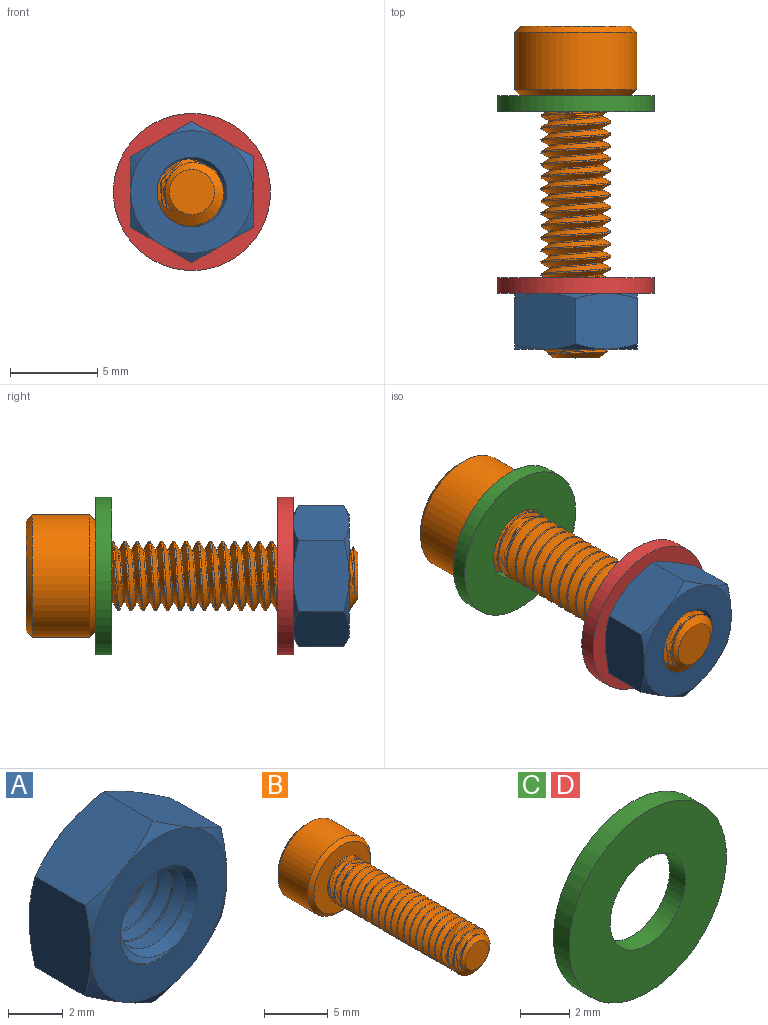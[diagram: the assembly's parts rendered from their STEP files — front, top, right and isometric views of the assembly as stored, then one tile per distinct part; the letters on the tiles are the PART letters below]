
ASSEMBLY  parts=4 mates=3
PART A: 26 faces, bbox 8.4x4.2x8.4 mm
  f0: plane 3.83x3.54mm, normal (-0.5,0,0.87), area 12.1mm2, adj f1,f5,f17,f18,f21,f22
  f1: plane 4.38x3.54mm, normal (-1,0,0), area 12.1mm2, adj f0,f2,f16,f17,f22,f23
  f2: plane 3.83x3.54mm, normal (-0.5,0,-0.87), area 12.1mm2, adj f1,f3,f15,f16,f23,f24
  f3: plane 3.83x3.54mm, normal (0.5,0,-0.87), area 12.1mm2, adj f2,f4,f14,f15,f24,f25
  f4: plane 4.38x3.54mm, normal (1,0,0), area 12.1mm2, adj f3,f5,f14,f19,f20,f25
  f5: plane 3.83x3.54mm, normal (0.5,0,0.87), area 12.1mm2, adj f0,f4,f18,f19,f20,f21
  f6: plane 7x7mm, normal (0,-1,0), area 25.9mm2, adj f8,f13,f14,f15,f16,f17,f18,f19
  f7: plane 7x7mm, normal (0,1,0), area 25.9mm2, adj f9,f13,f20,f21,f22,f23,f24,f25
  f8: cone r=2mm half-angle=45deg, axis (0,-1,0), area 3.7mm2, adj f6,f10,f11,f12
  f9: cone r=2mm half-angle=45deg, axis (0,1,0), area 3.7mm2, adj f7,f10,f11,f12
  f10: bspline ~4.62x4mm, area 23.1mm2, adj f8,f9,f12,f13
  f11: bspline ~4.62x4mm, area 23.1mm2, adj f8,f9,f12,f13
  f12: cylinder r=1.55mm len=3.09mm, axis (0,1,0), area 2.7mm2, adj f8,f9,f10,f11
  f13: cylinder r=2mm len=4mm, axis (0,1,0), area 5.1mm2, adj f6,f7,f10,f11
  f14: cone r=3.5mm half-angle=60deg, axis (0,1,0), area 1.2mm2, adj f3,f4,f6
  f15: cone r=3.5mm half-angle=60deg, axis (0,1,0), area 1.2mm2, adj f2,f3,f6
  f16: cone r=3.5mm half-angle=60deg, axis (0,1,0), area 1.2mm2, adj f1,f2,f6
  f17: cone r=3.5mm half-angle=60deg, axis (0,1,0), area 1.2mm2, adj f0,f1,f6
  f18: cone r=3.5mm half-angle=60deg, axis (0,1,0), area 1.2mm2, adj f0,f5,f6
  f19: cone r=3.5mm half-angle=60deg, axis (0,1,0), area 1.2mm2, adj f4,f5,f6
  f20: cone r=3.5mm half-angle=60deg, axis (0,-1,0), area 1.2mm2, adj f4,f5,f7
  f21: cone r=3.5mm half-angle=60deg, axis (0,-1,0), area 1.2mm2, adj f0,f5,f7
  f22: cone r=3.5mm half-angle=60deg, axis (0,-1,0), area 1.2mm2, adj f0,f1,f7
  f23: cone r=3.5mm half-angle=60deg, axis (0,-1,0), area 1.2mm2, adj f1,f2,f7
  f24: cone r=3.5mm half-angle=60deg, axis (0,-1,0), area 1.2mm2, adj f2,f3,f7
  f25: cone r=3.5mm half-angle=60deg, axis (0,-1,0), area 1.2mm2, adj f3,f4,f7
PART B: 24 faces, bbox 7.7x19.8x7.7 mm
  f0: cylinder r=2mm len=14.5mm, axis (0,-1,0), area 40.7mm2, adj f1,f2,f4,f8
  f1: bspline ~15.43x4.62mm, area 122.5mm2, adj f0,f3,f4,f8
  f2: bspline ~15.2x4.62mm, area 122mm2, adj f0,f3,f4,f8
  f3: cylinder r=1.55mm len=14.82mm, axis (0,1,0), area 3mm2, adj f1,f2,f4,f8
  f4: cone r=1.29mm half-angle=55deg, axis (0,1,0), area 5.8mm2, adj f0,f1,f2,f3,f5
  f5: plane 2.58x2.58mm, normal (0,-1,0), area 5.2mm2, adj f4
  f6: cylinder r=3.5mm len=7mm, axis (0,-1,0), area 72.6mm2, adj f22,f23
  f7: plane 6.3x6.3mm, normal (0,1,0), area 21.7mm2, adj f9,f10,f11,f12,f13,f14,f22
  f8: plane 6.57x6.57mm, normal (0,-1,0), area 21.2mm2, adj f0,f1,f2,f3,f23
  f9: cone r=1.73mm half-angle=45deg, axis (0,1,0), area 0mm2, adj f7,f16
  f10: cone r=1.73mm half-angle=45deg, axis (0,1,0), area 0mm2, adj f7,f17
  f11: cone r=1.73mm half-angle=45deg, axis (0,1,0), area 0mm2, adj f7,f18
  f12: cone r=1.73mm half-angle=45deg, axis (0,1,0), area 0mm2, adj f7,f19
  f13: cone r=1.73mm half-angle=45deg, axis (0,1,0), area 0mm2, adj f7,f20
  f14: cone r=1.73mm half-angle=45deg, axis (0,1,0), area 0mm2, adj f7,f21
  f15: plane 3.46x3mm, normal (0,1,0), area 7.8mm2, adj f16,f17,f18,f19,f20,f21
  f16: plane 2.91x2.16mm, normal (-0.5,0,-0.87), area 3.6mm2, adj f9,f15,f17,f21
  f17: plane 2.91x2.39mm, normal (-1,0,0), area 3.6mm2, adj f10,f15,f16,f18
  f18: plane 2.91x2.16mm, normal (-0.5,0,0.87), area 3.6mm2, adj f11,f15,f17,f19
  f19: plane 2.91x2.16mm, normal (0.5,0,0.87), area 3.6mm2, adj f12,f15,f18,f20
  f20: plane 2.91x2.39mm, normal (1,0,0), area 3.6mm2, adj f13,f15,f19,f21
  f21: plane 2.91x2.16mm, normal (0.5,0,-0.87), area 3.6mm2, adj f14,f15,f16,f20
  f22: cone r=3.15mm half-angle=45deg, axis (0,-1,0), area 10.3mm2, adj f6,f7
  f23: cone r=3.5mm half-angle=45deg, axis (0,1,0), area 10.3mm2, adj f6,f8
PART C: 4 faces, bbox 9x0.9x9 mm
  f0: plane 9x9mm, normal (0,-1,0), area 49.1mm2, adj f2,f3
  f1: plane 9x9mm, normal (0,1,0), area 49.1mm2, adj f2,f3
  f2: cylinder r=4.5mm len=9mm, axis (0,1,0), area 25.4mm2, adj f0,f1
  f3: cylinder r=2.15mm len=4.3mm, axis (0,1,0), area 12.2mm2, adj f0,f1
PART D: same geometry as C
PLACE A t=(-8.5,-5.46,1.71)mm
PLACE B t=(-8.5,-7.56,1.71)mm
PLACE C t=(-8.5,7.44,1.71)mm
PLACE D t=(-8.5,-2.96,1.71)mm
MATE fastened C.f2 <-> B.f0  axis (0,1,0) through (-8.5,7.44,1.71)mm
MATE fastened D.f2 <-> A.f8  axis (0,-1,0) through (-8.5,-3.86,1.71)mm
MATE fastened C.f2 <-> D.f2  axis (0,-1,0) through (-8.5,6.54,1.71)mm
